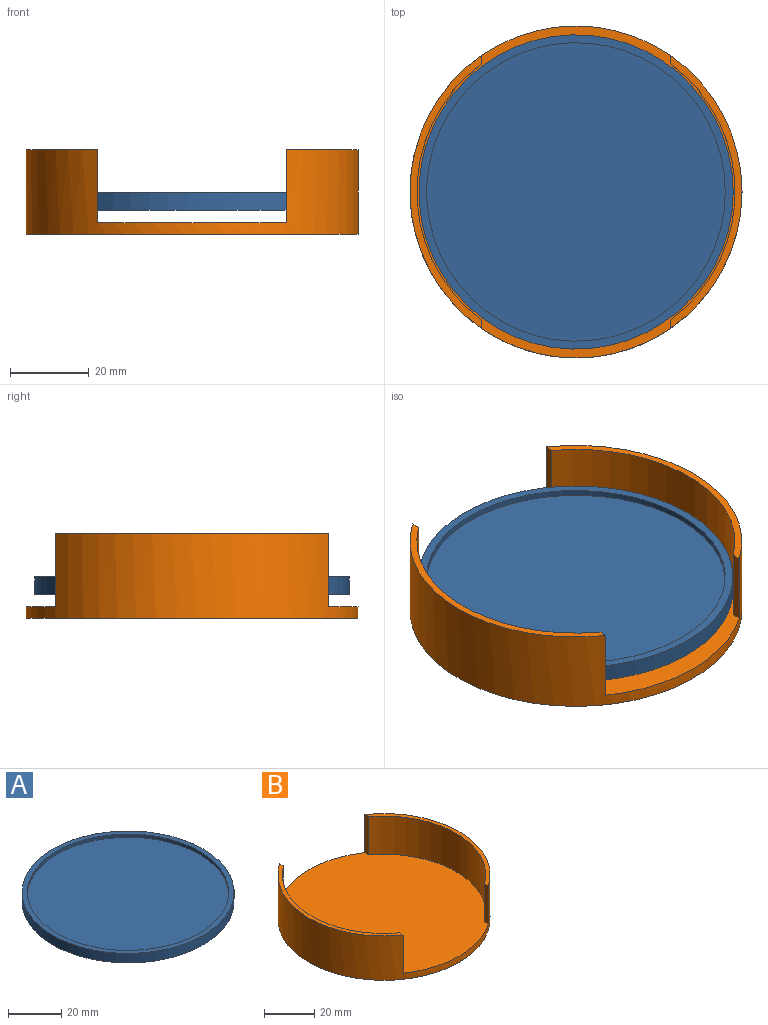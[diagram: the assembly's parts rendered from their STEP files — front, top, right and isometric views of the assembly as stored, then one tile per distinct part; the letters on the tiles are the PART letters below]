
ASSEMBLY  parts=2 mates=1
PART A: 5 faces, bbox 80x80x4.4 mm
  f0: cylinder r=40mm len=80mm, axis (0,0,-1), area 1105.8mm2, adj f1,f3
  f1: plane 80x80mm, normal (0,0,-1), area 5026.5mm2, adj f0
  f2: cylinder r=38mm len=76mm, axis (0,0,-1), area 358.1mm2, adj f3,f4
  f3: plane 80x80mm, normal (0,0,1), area 490.1mm2, adj f0,f2
  f4: plane 76x76mm, normal (0,0,1), area 4536.5mm2, adj f2
PART B: 11 faces, bbox 84.5x84.5x21.6 mm
  f0: plane 84.5x81mm, normal (0,0,1), area 5332.2mm2, adj f1,f3,f4,f5,f7,f8,f9
  f1: cylinder r=42.25mm len=84.5mm, axis (0,0,-1), area 3835mm2, adj f0,f2,f3,f4,f6,f7,f9,f10
  f2: plane 84.5x84.5mm, normal (0,0,-1), area 5607.9mm2, adj f1
  f3: plane 18.6x2.15mm, normal (1,0,0), area 40mm2, adj f0,f1,f5,f6
  f4: plane 18.6x2.15mm, normal (1,0,0), area 40mm2, adj f0,f1,f5,f6
  f5: cylinder r=40.5mm len=65.25mm, axis (0,0,-1), area 1411mm2, adj f0,f3,f4,f6
  f6: plane 69.54x18.25mm, normal (0,0,1), area 137.9mm2, adj f1,f3,f4,f5
  f7: plane 18.6x2.15mm, normal (-1,0,0), area 40mm2, adj f0,f1,f8,f10
  f8: cylinder r=40.5mm len=65.25mm, axis (0,0,-1), area 1411mm2, adj f0,f7,f9,f10
  f9: plane 18.6x2.15mm, normal (-1,0,0), area 40mm2, adj f0,f1,f8,f10
  f10: plane 69.54x18.25mm, normal (0,0,1), area 137.9mm2, adj f1,f7,f8,f9
PLACE A t=(-2.65,21.25,-5.47)mm
PLACE B t=(-2.65,21.25,-11.63)mm
MATE cylindrical A.f2 <-> B.f1  axis (0,0,1) through (-2.65,21.25,-1.07)mm
